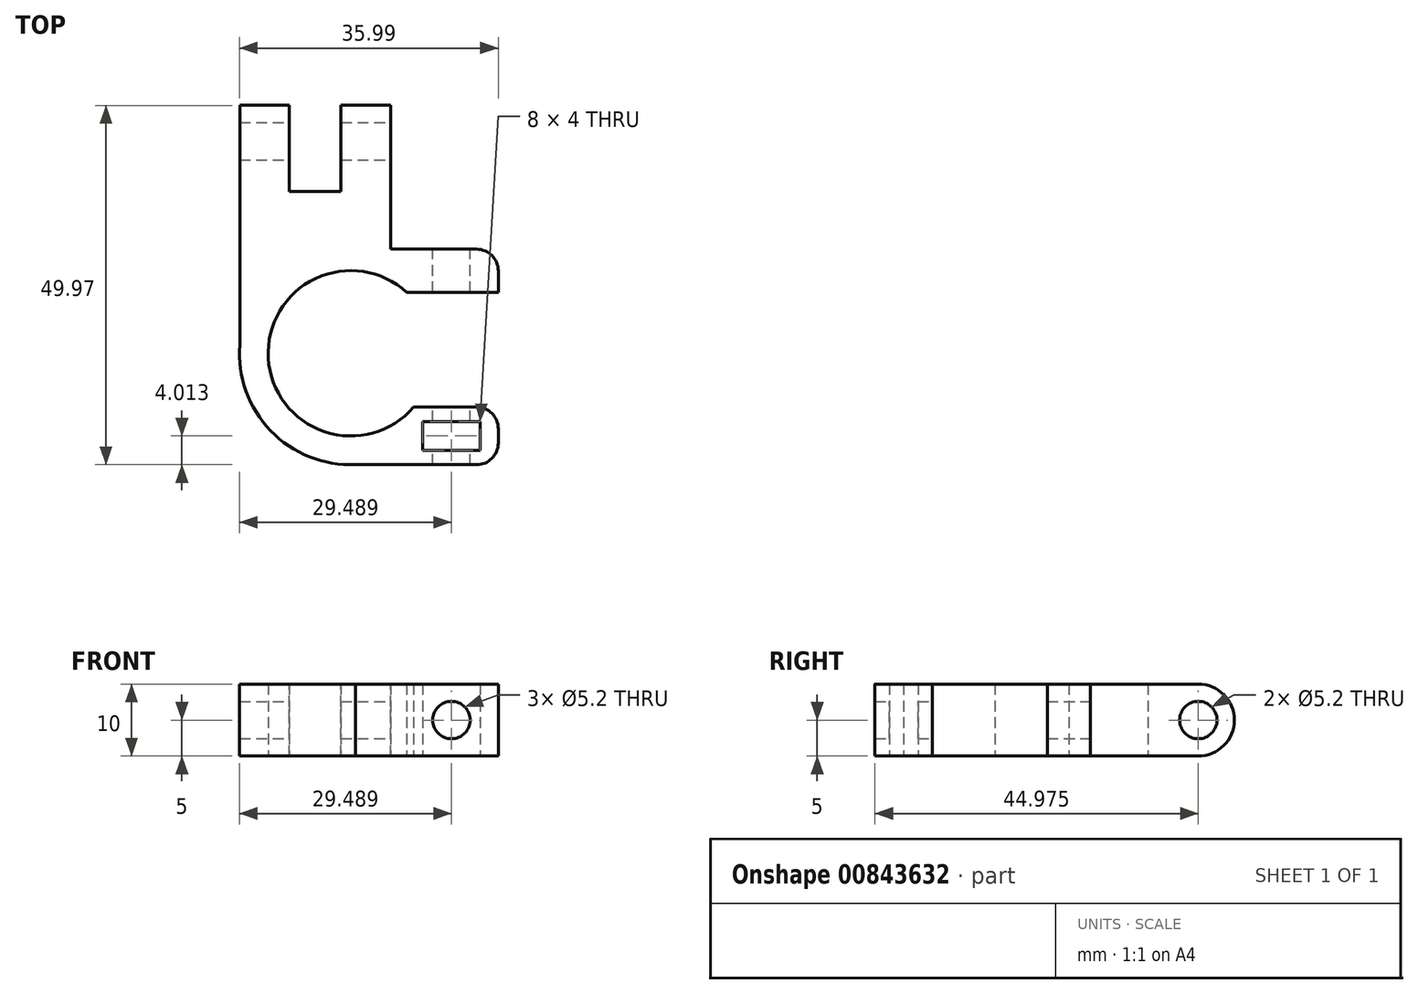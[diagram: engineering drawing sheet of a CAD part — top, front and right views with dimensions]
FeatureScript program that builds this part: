
annotation { "Feature Type Name" : "Feature", "Feature Type Description" : "" }
export const myFeature = defineFeature(function(context is Context, id is Id, definition is map)
    precondition{}
    {
        {
            var Q0;
            Q0=qCreatedBy(makeId("Top.planeOp"),FACE);
            var sketch = newSketch(context, id + "F0", { "sketchPlane" : qUnion([Q0])});
            skLineSegment(sketch, "E0", {"start": v(5.54, 14.47) * mm, "end": v(5.54, 14.47) * mm});
            skLineSegment(sketch, "E1.rect.top", {"start": v(20.49, 14.47) * mm, "end": v(5.54, 14.47) * mm});
            skLineSegment(sketch, "E1.rect.left", {"start": v(20.49, -15.49) * mm, "end": v(20.49, -7.49) * mm});
            skLineSegment(sketch, "E2.0", {"start": v(20.49, 8.47) * mm, "end": v(7.77, 8.47) * mm});
            skLineSegment(sketch, "E3.0", {"start": v(20.49, -7.49) * mm, "end": v(8.73, -7.49) * mm});
            skLineSegment(sketch, "E4.trimOffspring", {"start": v(20.49, 8.47) * mm, "end": v(20.49, 14.47) * mm});
            skCircle(sketch, "E5.converted", {"center": v(0, 0) * mm, "radius": 11.5 * mm, "construction": true});
            skArc(sketch, "E6.0", {"start": v(7.77, 8.47) * mm, "mid": v(-11.48, -0.69) * mm, "end": v(8.73, -7.49) * mm});
            skLineSegment(sketch, "E7.rect.bottom", {"start": v(-15.46, 34.47) * mm, "end": v(-8.56, 34.47) * mm});
            skLineSegment(sketch, "E7.rect.left", {"start": v(-15.46, 34.47) * mm, "end": v(-15.46, 1.16) * mm});
            skLineSegment(sketch, "E7.rect.right", {"start": v(5.54, 34.47) * mm, "end": v(5.54, 14.47) * mm});
            skPoint(sketch, "E7.rect.middle", {"position": v(0.06, 0.12) * mm});
            skLineSegment(sketch, "E8.0", {"start": v(-8.56, 22.47) * mm, "end": v(-1.36, 22.47) * mm});
            skLineSegment(sketch, "E9.0", {"start": v(-8.56, 34.47) * mm, "end": v(-8.56, 22.47) * mm});
            skLineSegment(sketch, "E10.0", {"start": v(-1.36, 34.47) * mm, "end": v(-1.36, 22.47) * mm});
            skArc(sketch, "E11.trimOffspring", {"start": v(-15.46, 1.16) * mm, "mid": v(-11.15, -10.77) * mm, "end": v(0.62, -15.49) * mm});
            skLineSegment(sketch, "E12.trimOffspring", {"start": v(-1.36, 34.47) * mm, "end": v(5.54, 34.47) * mm});
            skLineSegment(sketch, "E13.0", {"start": v(20.49, -15.49) * mm, "end": v(11.59, -15.49) * mm});
            skLineSegment(sketch, "E14", {"start": v(11.59, -15.49) * mm, "end": v(0.62, -15.49) * mm});
            skLineSegment(sketch, "E15.0", {"start": v(17.99, -13.49) * mm, "end": v(17.99, -9.49) * mm});
            skLineSegment(sketch, "E16.0", {"start": v(9.99, -13.49) * mm, "end": v(9.99, -9.49) * mm});
            skLineSegment(sketch, "E17", {"start": v(20.49, -7.49) * mm, "end": v(20.49, 8.47) * mm, "construction": true});
            skLineSegment(sketch, "E18.0", {"start": v(17.99, -13.49) * mm, "end": v(9.99, -13.49) * mm});
            skLineSegment(sketch, "E19.0", {"start": v(17.99, -9.49) * mm, "end": v(9.99, -9.49) * mm});
            skLineSegment(sketch, "E20", {"start": v(20.49, 0.5) * mm, "end": v(11.49, 0.5) * mm, "construction": true});
            skSolve(sketch);
        }
        {
            var Q0;
            Q0=qSketchRegion(id+"F0",true);
            extrude(context, id + "F1", {"entities" : qUnion([Q0]), "depth" : 10 * mm});
        }
        {
            var Q0;
            Q0=makeQuery(id+"F1.opExtrude","SWEPT_FACE",FACE,{"disambiguationData":[OSD([sQuery(id+"F0.wireOp",EDGE,"E7.rect.right")])]});
            var sketch = newSketch(context, id + "F2", { "sketchPlane" : qUnion([Q0])});
            skLineSegment(sketch, "E21.0.0", {"start": v(29.47, 0) * mm, "end": v(34.47, 0) * mm});
            skLineSegment(sketch, "E21.0.1", {"start": v(34.47, 0) * mm, "end": v(34.47, 10) * mm});
            skLineSegment(sketch, "E21.0.2", {"start": v(34.47, 10) * mm, "end": v(29.47, 10) * mm});
            skCircle(sketch, "E22", {"center": v(29.47, 5) * mm, "radius": 2.6 * mm});
            skPoint(sketch, "E22.centerSnap0", {"position": v(29.47, 10) * mm});
            skArc(sketch, "E23", {"start": v(29.47, 0) * mm, "mid": v(34.47, 5) * mm, "end": v(29.47, 10) * mm});
            skSolve(sketch);
        }
        {
            var Q0;
            Q0=qSketchRegion(id+"F2",true);
            var Q1;
            Q1=makeQuery(id+"F1.opExtrude","SWEPT_FACE",FACE,{"disambiguationData":[OSD([sQuery(id+"F0.wireOp",EDGE,"E7.rect.left")])]});
            extrude(context, id + "F3", {"entities" : qUnion([Q0]), "operationType" : NewBodyOperationType.REMOVE, "endBound" : BoundingType.UP_TO_SURFACE, "oppositeDirection" : true, "endBoundEntityFace" : qUnion([Q1]), "depth" : 25 * mm});
        }
        {
            var Q0;
            Q0=makeQuery(id+"F1.opExtrude","SWEPT_FACE",FACE,{"disambiguationData":[OSD([sQuery(id+"F0.wireOp",EDGE,"E18.0")])]});
            var sketch = newSketch(context, id + "F4", { "sketchPlane" : qUnion([Q0])});
            skLineSegment(sketch, "E24.0.0", {"start": v(-17.99, 0) * mm, "end": v(-9.99, 0) * mm, "construction": true});
            skLineSegment(sketch, "E24.0.1", {"start": v(-9.99, 0) * mm, "end": v(-9.99, 10) * mm, "construction": true});
            skLineSegment(sketch, "E24.0.2", {"start": v(-9.99, 10) * mm, "end": v(-17.99, 10) * mm, "construction": true});
            skLineSegment(sketch, "E24.0.3", {"start": v(-17.99, 10) * mm, "end": v(-17.99, 0) * mm, "construction": true});
            skCircle(sketch, "E25", {"center": v(-13.99, 5) * mm, "radius": 2.6 * mm});
            skPoint(sketch, "E25.centerSnap0", {"position": v(-9.99, 5) * mm});
            skPoint(sketch, "E25.centerSnap1", {"position": v(-13.99, 10) * mm});
            skSolve(sketch);
        }
        {
            var Q0;
            Q0=qSketchRegion(id+"F4",true);
            extrude(context, id + "F5", {"entities" : qUnion([Q0]), "operationType" : NewBodyOperationType.REMOVE, "oppositeDirection" : true, "depth" : 100 * mm, "symmetric" : true});
        }
        {
            var Q0;
            Q0=makeQuery(id+"F1.opExtrude","SWEPT_EDGE",EDGE,{"disambiguationData":[OSD([sQuery(id+"F0.wireOp",EDGE,"E1.rect.top"),sQuery(id+"F0.wireOp",EDGE,"E4.trimOffspring")])]});
            var Q1;
            Q1=makeQuery(id+"F1.opExtrude","SWEPT_EDGE",EDGE,{"disambiguationData":[OSD([sQuery(id+"F0.wireOp",EDGE,"E1.rect.left"),sQuery(id+"F0.wireOp",EDGE,"E3.0")])]});
            var Q2;
            Q2=makeQuery(id+"F1.opExtrude","SWEPT_EDGE",EDGE,{"disambiguationData":[OSD([sQuery(id+"F0.wireOp",EDGE,"E1.rect.left"),sQuery(id+"F0.wireOp",EDGE,"E13.0")])]});
            fillet(context, id + "F6", {"entities" : qUnion([Q0, Q1, Q2]), "radius" : 3 * mm, "tangentPropagation" : true, "allowEdgeOverflow" : false});
        }
    });
